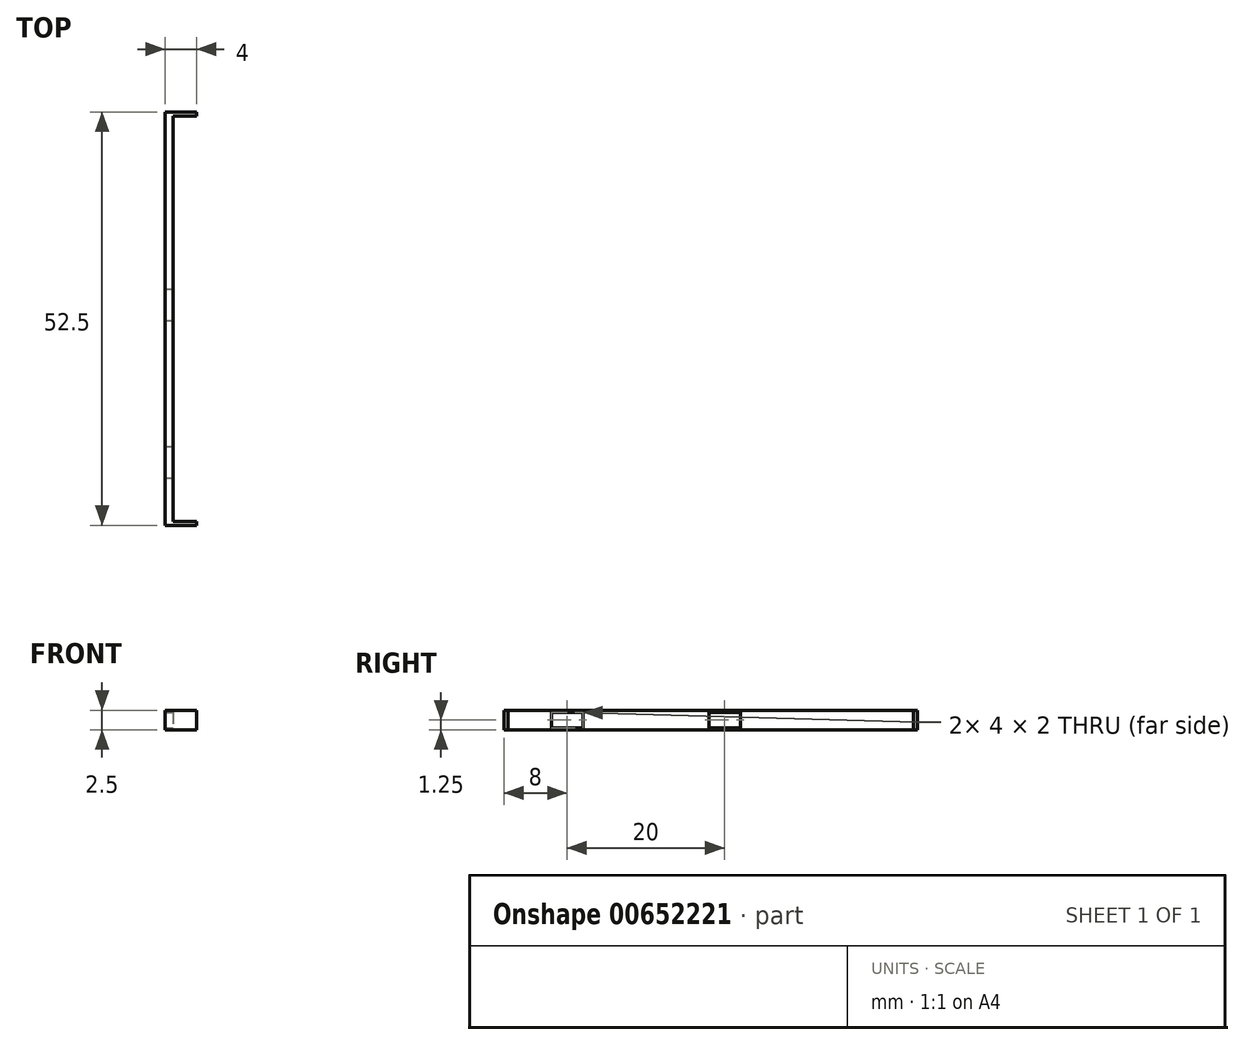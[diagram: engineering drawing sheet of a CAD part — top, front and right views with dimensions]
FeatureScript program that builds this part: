
annotation { "Feature Type Name" : "Feature", "Feature Type Description" : "" }
export const myFeature = defineFeature(function(context is Context, id is Id, definition is map)
    precondition{}
    {
        {
            var Q0;
            Q0=qCreatedBy(makeId("Right.planeOp"),FACE);
            var sketch = newSketch(context, id + "F0", { "sketchPlane" : qUnion([Q0])});
            skLineSegment(sketch, "E0.bottom", {"start": v(-26.25, 1.25) * mm, "end": v(26.25, 1.25) * mm});
            skLineSegment(sketch, "E0.top", {"start": v(-26.25, -1.25) * mm, "end": v(26.25, -1.25) * mm});
            skLineSegment(sketch, "E0.left", {"start": v(-26.25, 1.25) * mm, "end": v(-26.25, -1.25) * mm});
            skLineSegment(sketch, "E0.right", {"start": v(26.25, 1.25) * mm, "end": v(26.25, -1.25) * mm});
            skPoint(sketch, "E0.middle", {"position": v(0, 0) * mm});
            skSolve(sketch);
        }
        {
            var Q0;
            Q0=qSketchRegion(id+"F0",true);
            extrude(context, id + "F1", {"entities" : qUnion([Q0]), "depth" : 1 * mm, "offsetDistance" : 25 * mm});
        }
        {
            var Q0;
            Q0=makeQuery(id+"F1.opExtrude","CAP_FACE",FACE,{"disambiguationData":[OSD([sQuery(id+"F0.wireOp",EDGE,"E0.bottom"),sQuery(id+"F0.wireOp",EDGE,"E0.top"),sQuery(id+"F0.wireOp",EDGE,"E0.left"),sQuery(id+"F0.wireOp",EDGE,"E0.right")])],"isStart":false});
            var sketch = newSketch(context, id + "F2", { "sketchPlane" : qUnion([Q0])});
            skLineSegment(sketch, "E1.bottom", {"start": v(-26.25, 1.25) * mm, "end": v(-25.75, 1.25) * mm});
            skLineSegment(sketch, "E1.top", {"start": v(-26.25, -1.25) * mm, "end": v(-25.75, -1.25) * mm});
            skLineSegment(sketch, "E1.left", {"start": v(-26.25, 1.25) * mm, "end": v(-26.25, -1.25) * mm});
            skLineSegment(sketch, "E1.right", {"start": v(-25.75, 1.25) * mm, "end": v(-25.75, -1.25) * mm});
            skLineSegment(sketch, "E2.bottom", {"start": v(26.25, 1.25) * mm, "end": v(25.75, 1.25) * mm});
            skLineSegment(sketch, "E2.top", {"start": v(26.25, -1.25) * mm, "end": v(25.75, -1.25) * mm});
            skLineSegment(sketch, "E2.left", {"start": v(26.25, 1.25) * mm, "end": v(26.25, -1.25) * mm});
            skLineSegment(sketch, "E2.right", {"start": v(25.75, 1.25) * mm, "end": v(25.75, -1.25) * mm});
            skSolve(sketch);
        }
        {
            var Q0;
            Q0=qSketchRegion(id+"F2",true);
            extrude(context, id + "F3", {"entities" : qUnion([Q0]), "operationType" : NewBodyOperationType.ADD, "depth" : 3 * mm, "offsetDistance" : 25 * mm});
        }
        {
            var Q0;
            Q0=makeQuery(id+"F1.opExtrude","CAP_FACE",FACE,{"disambiguationData":[OSD([sQuery(id+"F0.wireOp",EDGE,"E0.bottom"),sQuery(id+"F0.wireOp",EDGE,"E0.top"),sQuery(id+"F0.wireOp",EDGE,"E0.left"),sQuery(id+"F0.wireOp",EDGE,"E0.right")])],"isStart":false});
            var sketch = newSketch(context, id + "F4", { "sketchPlane" : qUnion([Q0])});
            skLineSegment(sketch, "E3.bottom", {"start": v(-20.25, 1) * mm, "end": v(-16.25, 1) * mm});
            skLineSegment(sketch, "E3.top", {"start": v(-20.25, -1) * mm, "end": v(-16.25, -1) * mm});
            skLineSegment(sketch, "E3.left", {"start": v(-20.25, 1) * mm, "end": v(-20.25, -1) * mm});
            skLineSegment(sketch, "E3.right", {"start": v(-16.25, 1) * mm, "end": v(-16.25, -1) * mm});
            skPoint(sketch, "E3.middle", {"position": v(-18.25, 0) * mm});
            skLineSegment(sketch, "E4.bottom", {"start": v(3.75, 1) * mm, "end": v(-0.25, 1) * mm});
            skLineSegment(sketch, "E4.top", {"start": v(3.75, -1) * mm, "end": v(-0.25, -1) * mm});
            skLineSegment(sketch, "E4.left", {"start": v(3.75, 1) * mm, "end": v(3.75, -1) * mm});
            skLineSegment(sketch, "E4.right", {"start": v(-0.25, 1) * mm, "end": v(-0.25, -1) * mm});
            skPoint(sketch, "E4.middle", {"position": v(1.75, 0) * mm});
            skSolve(sketch);
        }
        {
            var Q0;
            Q0=qSketchRegion(id+"F4",true);
            extrude(context, id + "F5", {"entities" : qUnion([Q0]), "operationType" : NewBodyOperationType.REMOVE, "endBound" : BoundingType.UP_TO_NEXT, "oppositeDirection" : true, "depth" : 25 * mm, "offsetDistance" : 25 * mm});
        }
    });
